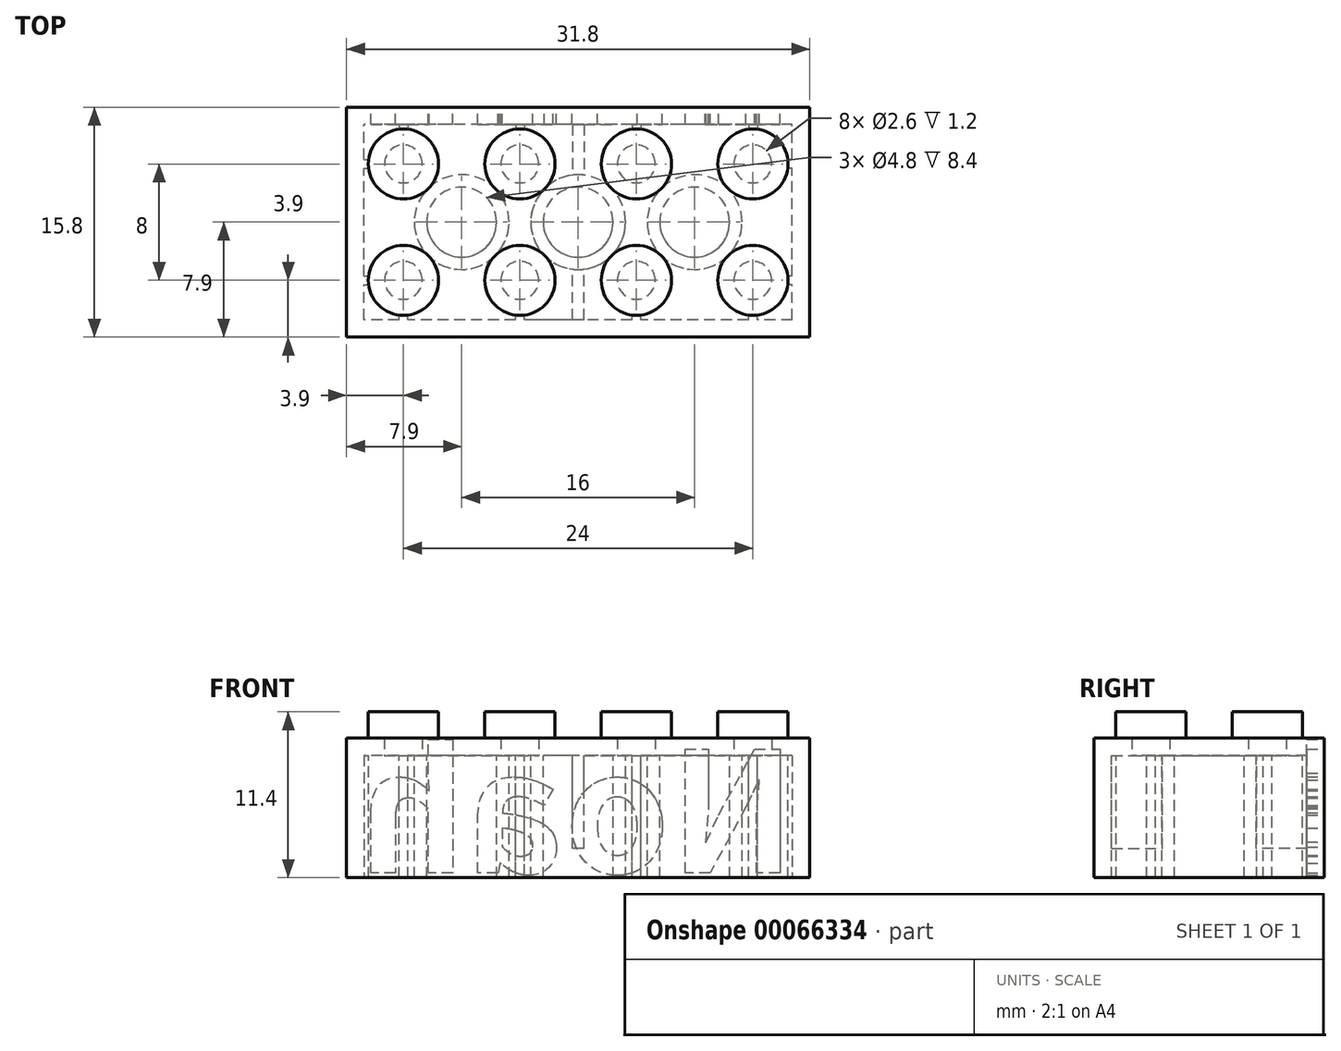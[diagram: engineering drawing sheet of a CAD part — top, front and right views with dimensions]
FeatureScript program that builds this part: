
annotation { "Feature Type Name" : "Feature", "Feature Type Description" : "" }
export const myFeature = defineFeature(function(context is Context, id is Id, definition is map)
    precondition{}
    {
        {
            var Q0;
            Q0=qCreatedBy(makeId("Top.planeOp"),FACE);
            var sketch = newSketch(context, id + "F0", { "sketchPlane" : qUnion([Q0])});
            skLineSegment(sketch, "E0.bottom", {"start": v(-15.9, -7.9) * mm, "end": v(15.9, -7.9) * mm});
            skLineSegment(sketch, "E0.top", {"start": v(-15.9, 7.9) * mm, "end": v(15.9, 7.9) * mm});
            skLineSegment(sketch, "E0.left", {"start": v(-15.9, -7.9) * mm, "end": v(-15.9, 7.9) * mm});
            skLineSegment(sketch, "E0.right", {"start": v(15.9, -7.9) * mm, "end": v(15.9, 7.9) * mm});
            skSolve(sketch);
        }
        {
            var Q0;
            Q0 = qSketchRegion(id + "F0", true);
            extrude(context, id + "F1", {"entities" : qUnion([Q0]), "endBound" : BoundingType.SYMMETRIC, "oppositeDirection" : true, "depth" : 9.6 * mm, "offsetDistance" : 25 * mm});
        }
        {
            var Q0;
            Q0=makeQuery(id+"F1.opExtrude","CAP_FACE",FACE,{"disambiguationData":[OSD([sQuery(id+"F0.wireOp",EDGE,"E0.bottom"),sQuery(id+"F0.wireOp",EDGE,"E0.top"),sQuery(id+"F0.wireOp",EDGE,"E0.left"),sQuery(id+"F0.wireOp",EDGE,"E0.right")])],"isStart":false});
            var sketch = newSketch(context, id + "F2", { "sketchPlane" : qUnion([Q0])});
            skLineSegment(sketch, "E1.bottom", {"start": v(14.7, 6.7) * mm, "end": v(-14.7, 6.7) * mm});
            skLineSegment(sketch, "E1.top", {"start": v(14.7, -6.7) * mm, "end": v(-14.7, -6.7) * mm});
            skLineSegment(sketch, "E1.left", {"start": v(14.7, 6.7) * mm, "end": v(14.7, -6.7) * mm});
            skLineSegment(sketch, "E1.right", {"start": v(-14.7, 6.7) * mm, "end": v(-14.7, -6.7) * mm});
            skPoint(sketch, "E1.middle", {"position": v(0, 0) * mm});
            skSolve(sketch);
        }
        {
            var Q0;
            Q0 = qSketchRegion(id + "F2", true);
            extrude(context, id + "F3", {"entities" : qUnion([Q0]), "operationType" : NewBodyOperationType.REMOVE, "oppositeDirection" : true, "depth" : 8.4 * mm, "offsetDistance" : 25 * mm});
        }
        {
            var Q0;
            Q0=makeQuery(id+"F1.opExtrude","CAP_FACE",FACE,{"disambiguationData":[OSD([sQuery(id+"F0.wireOp",EDGE,"E0.bottom"),sQuery(id+"F0.wireOp",EDGE,"E0.top"),sQuery(id+"F0.wireOp",EDGE,"E0.left"),sQuery(id+"F0.wireOp",EDGE,"E0.right")])],"isStart":true});
            var sketch = newSketch(context, id + "F4", { "sketchPlane" : qUnion([Q0])});
            skCircle(sketch, "E2", {"center": v(-12, 4) * mm, "radius": 2.4 * mm});
            skCircle(sketch, "E3", {"center": v(-4, 4) * mm, "radius": 2.4 * mm});
            skCircle(sketch, "E4.MirrorC", {"center": v(-12, -4) * mm, "radius": 2.4 * mm});
            skCircle(sketch, "E5.MirrorC", {"center": v(-4, -4) * mm, "radius": 2.4 * mm});
            skCircle(sketch, "E6.MirrorC", {"center": v(4, -4) * mm, "radius": 2.4 * mm});
            skCircle(sketch, "E7.MirrorC", {"center": v(12, -4) * mm, "radius": 2.4 * mm});
            skCircle(sketch, "E8.MirrorC", {"center": v(4, 4) * mm, "radius": 2.4 * mm});
            skCircle(sketch, "E9.MirrorC", {"center": v(12, 4) * mm, "radius": 2.4 * mm});
            skSolve(sketch);
        }
        {
            var Q0;
            Q0 = qSketchRegion(id + "F4", true);
            extrude(context, id + "F5", {"entities" : qUnion([Q0]), "operationType" : NewBodyOperationType.ADD, "depth" : 1.8 * mm, "offsetDistance" : 25 * mm});
        }
        {
            var Q0;
            Q0=makeQuery(id+"F3.boolean.opBoolean","COPY",FACE,{"derivedFrom":makeQuery(id+"F3.opExtrude","CAP_FACE",FACE,{"disambiguationData":[OSD([sQuery(id+"F2.wireOp",EDGE,"E1.bottom"),sQuery(id+"F2.wireOp",EDGE,"E1.top"),sQuery(id+"F2.wireOp",EDGE,"E1.left"),sQuery(id+"F2.wireOp",EDGE,"E1.right")])],"isStart":false})});
            var sketch = newSketch(context, id + "F6", { "sketchPlane" : qUnion([Q0])});
            skCircle(sketch, "E10", {"center": v(-12, 4) * mm, "radius": 1.3 * mm});
            skCircle(sketch, "E11", {"center": v(-4, 4) * mm, "radius": 1.3 * mm});
            skCircle(sketch, "E12.MirrorC", {"center": v(-12, -4) * mm, "radius": 1.3 * mm});
            skCircle(sketch, "E13.MirrorC", {"center": v(-4, -4) * mm, "radius": 1.3 * mm});
            skCircle(sketch, "E14.MirrorC", {"center": v(4, -4) * mm, "radius": 1.3 * mm});
            skCircle(sketch, "E15.MirrorC", {"center": v(12, -4) * mm, "radius": 1.3 * mm});
            skCircle(sketch, "E16.MirrorC", {"center": v(4, 4) * mm, "radius": 1.3 * mm});
            skCircle(sketch, "E17.MirrorC", {"center": v(12, 4) * mm, "radius": 1.3 * mm});
            skSolve(sketch);
        }
        {
            var Q0;
            Q0 = qSketchRegion(id + "F6", true);
            extrude(context, id + "F7", {"entities" : qUnion([Q0]), "operationType" : NewBodyOperationType.REMOVE, "oppositeDirection" : true, "depth" : 1.2 * mm, "offsetDistance" : 25 * mm});
        }
        {
            var Q0;
            Q0=makeQuery(id+"F3.boolean.opBoolean","COPY",FACE,{"derivedFrom":makeQuery(id+"F3.opExtrude","CAP_FACE",FACE,{"disambiguationData":[OSD([sQuery(id+"F2.wireOp",EDGE,"E1.bottom"),sQuery(id+"F2.wireOp",EDGE,"E1.top"),sQuery(id+"F2.wireOp",EDGE,"E1.left"),sQuery(id+"F2.wireOp",EDGE,"E1.right")])],"isStart":false})});
            var sketch = newSketch(context, id + "F8", { "sketchPlane" : qUnion([Q0])});
            skPoint(sketch, "E18", {"position": v(-12, 4) * mm});
            skPoint(sketch, "E19", {"position": v(-12, -4) * mm});
            skPoint(sketch, "E20", {"position": v(-4, 4) * mm});
            skPoint(sketch, "E21", {"position": v(-4, -4) * mm});
            skPoint(sketch, "E22", {"position": v(4, 4) * mm});
            skPoint(sketch, "E23", {"position": v(4, -4) * mm});
            skPoint(sketch, "E24", {"position": v(12, 4) * mm});
            skPoint(sketch, "E25", {"position": v(12, -4) * mm});
            skLineSegment(sketch, "E26", {"start": v(-12, 4) * mm, "end": v(-4, -4) * mm, "construction": true});
            skLineSegment(sketch, "E27", {"start": v(-12, -4) * mm, "end": v(-4, 4) * mm, "construction": true});
            skLineSegment(sketch, "E28", {"start": v(-4, 4) * mm, "end": v(4, -4) * mm, "construction": true});
            skLineSegment(sketch, "E29", {"start": v(-4, -4) * mm, "end": v(4, 4) * mm, "construction": true});
            skLineSegment(sketch, "E30", {"start": v(4, 4) * mm, "end": v(12, -4) * mm, "construction": true});
            skLineSegment(sketch, "E31", {"start": v(4, -4) * mm, "end": v(12, 4) * mm, "construction": true});
            skCircle(sketch, "E32", {"center": v(-8, 0) * mm, "radius": 3.25 * mm});
            skCircle(sketch, "E33", {"center": v(0, 0) * mm, "radius": 3.25 * mm});
            skCircle(sketch, "E34", {"center": v(8, 0) * mm, "radius": 3.25 * mm});
            skCircle(sketch, "E35", {"center": v(-8, 0) * mm, "radius": 2.4 * mm});
            skCircle(sketch, "E36", {"center": v(0, 0) * mm, "radius": 2.4 * mm});
            skCircle(sketch, "E37", {"center": v(8, 0) * mm, "radius": 2.4 * mm});
            skSolve(sketch);
        }
        {
            var Q0;
            Q0 = qSketchRegion(id + "F8", true);
            var Q1;
            Q1=makeQuery(id+"F1.opExtrude","CAP_FACE",FACE,{"disambiguationData":[OSD([sQuery(id+"F0.wireOp",EDGE,"E0.bottom"),sQuery(id+"F0.wireOp",EDGE,"E0.top"),sQuery(id+"F0.wireOp",EDGE,"E0.left"),sQuery(id+"F0.wireOp",EDGE,"E0.right")])],"isStart":false});
            extrude(context, id + "F9", {"entities" : qUnion([Q0]), "operationType" : NewBodyOperationType.ADD, "endBound" : BoundingType.UP_TO_SURFACE, "depth" : 25 * mm, "endBoundEntityFace" : qUnion([Q1]), "offsetDistance" : 25 * mm});
        }
        {
            var Q0;
            {var subQ0=sQuery(id+"F2.wireOp",EDGE,"E1.left");var subQ1=sQuery(id+"F2.wireOp",EDGE,"E1.bottom");var subQ2=sQuery(id+"F2.wireOp",EDGE,"E1.top");var subQ3=sQuery(id+"F2.wireOp",EDGE,"E1.right");Q0=makeQuery(id+"F9.boolean.opBoolean","SPLIT",FACE,{"disambiguationData":[TD([makeQuery(id+"F3.boolean.opBoolean","COPY",FACE,{"derivedFrom":makeQuery(id+"F3.opExtrude","SWEPT_FACE",FACE,{"disambiguationData":[OSD([subQ1])]})})])],"derivedFrom":makeQuery(id+"F3.boolean.opBoolean","COPY",FACE,{"derivedFrom":makeQuery(id+"F3.opExtrude","CAP_FACE",FACE,{"disambiguationData":[OSD([subQ1,subQ2,subQ0,subQ3])],"isStart":false})})});}
            var sketch = newSketch(context, id + "F10", { "sketchPlane" : qUnion([Q0])});
            skPoint(sketch, "E38", {"position": v(-12, 4) * mm});
            skLineSegment(sketch, "E39", {"start": v(-12, 4) * mm, "end": v(-24.8, 4) * mm, "construction": true});
            skLineSegment(sketch, "E40.bottom", {"start": v(-14.7, 3.7) * mm, "end": v(-14.4, 3.7) * mm});
            skLineSegment(sketch, "E40.top", {"start": v(-14.7, 4.3) * mm, "end": v(-14.4, 4.3) * mm});
            skLineSegment(sketch, "E40.left", {"start": v(-14.7, 3.7) * mm, "end": v(-14.7, 4.3) * mm});
            skLineSegment(sketch, "E40.right", {"start": v(-14.4, 3.7) * mm, "end": v(-14.4, 4.3) * mm});
            skLineSegment(sketch, "E41.MirrorCS", {"start": v(-14.7, -4.3) * mm, "end": v(-14.4, -4.3) * mm});
            skLineSegment(sketch, "E42.MirrorCS", {"start": v(-14.7, -3.7) * mm, "end": v(-14.7, -4.3) * mm});
            skLineSegment(sketch, "E43.MirrorCS", {"start": v(-14.4, -3.7) * mm, "end": v(-14.4, -4.3) * mm});
            skLineSegment(sketch, "E44.MirrorCS", {"start": v(-14.7, -3.7) * mm, "end": v(-14.4, -3.7) * mm});
            skLineSegment(sketch, "E45.MirrorCS", {"start": v(14.7, 3.7) * mm, "end": v(14.7, 4.3) * mm});
            skLineSegment(sketch, "E46.MirrorCS", {"start": v(14.7, 4.3) * mm, "end": v(14.4, 4.3) * mm});
            skLineSegment(sketch, "E47.MirrorCS", {"start": v(14.4, 3.7) * mm, "end": v(14.4, 4.3) * mm});
            skLineSegment(sketch, "E48.MirrorCS", {"start": v(14.7, 3.7) * mm, "end": v(14.4, 3.7) * mm});
            skLineSegment(sketch, "E49.MirrorCS", {"start": v(14.7, -3.7) * mm, "end": v(14.7, -4.3) * mm});
            skLineSegment(sketch, "E50.MirrorCS", {"start": v(14.7, -3.7) * mm, "end": v(14.4, -3.7) * mm});
            skLineSegment(sketch, "E51.MirrorCS", {"start": v(14.4, -3.7) * mm, "end": v(14.4, -4.3) * mm});
            skLineSegment(sketch, "E52.MirrorCS", {"start": v(14.7, -4.3) * mm, "end": v(14.4, -4.3) * mm});
            skSolve(sketch);
        }
        {
            var Q0;
            Q0 = qSketchRegion(id + "F10", true);
            var Q1;
            Q1=makeQuery(id+"F1.opExtrude","CAP_FACE",FACE,{"disambiguationData":[OSD([sQuery(id+"F0.wireOp",EDGE,"E0.bottom"),sQuery(id+"F0.wireOp",EDGE,"E0.top"),sQuery(id+"F0.wireOp",EDGE,"E0.left"),sQuery(id+"F0.wireOp",EDGE,"E0.right")])],"isStart":false});
            extrude(context, id + "F11", {"entities" : qUnion([Q0]), "operationType" : NewBodyOperationType.ADD, "endBound" : BoundingType.UP_TO_SURFACE, "depth" : 25 * mm, "endBoundEntityFace" : qUnion([Q1]), "offsetDistance" : 25 * mm});
        }
        {
            var Q0;
            {var subQ0=sQuery(id+"F2.wireOp",EDGE,"E1.left");var subQ1=sQuery(id+"F2.wireOp",EDGE,"E1.bottom");var subQ2=sQuery(id+"F2.wireOp",EDGE,"E1.top");var subQ3=sQuery(id+"F2.wireOp",EDGE,"E1.right");Q0=makeQuery(id+"F9.boolean.opBoolean","SPLIT",FACE,{"disambiguationData":[TD([makeQuery(id+"F3.boolean.opBoolean","COPY",FACE,{"derivedFrom":makeQuery(id+"F3.opExtrude","SWEPT_FACE",FACE,{"disambiguationData":[OSD([subQ1])]})})])],"derivedFrom":makeQuery(id+"F3.boolean.opBoolean","COPY",FACE,{"derivedFrom":makeQuery(id+"F3.opExtrude","CAP_FACE",FACE,{"disambiguationData":[OSD([subQ1,subQ2,subQ0,subQ3])],"isStart":false})})});}
            var sketch = newSketch(context, id + "F12", { "sketchPlane" : qUnion([Q0])});
            skPoint(sketch, "E53", {"position": v(-12, 4) * mm});
            skLineSegment(sketch, "E54", {"start": v(-12, 4) * mm, "end": v(-12, 11.14) * mm, "construction": true});
            skLineSegment(sketch, "E55.bottom", {"start": v(-12.3, 6.7) * mm, "end": v(-11.7, 6.7) * mm});
            skLineSegment(sketch, "E55.top", {"start": v(-12.3, 6.4) * mm, "end": v(-11.7, 6.4) * mm});
            skLineSegment(sketch, "E55.left", {"start": v(-12.3, 6.7) * mm, "end": v(-12.3, 6.4) * mm});
            skLineSegment(sketch, "E55.right", {"start": v(-11.7, 6.7) * mm, "end": v(-11.7, 6.4) * mm});
            skPoint(sketch, "E56", {"position": v(-8, 0) * mm});
            skLineSegment(sketch, "E57", {"start": v(-8, 0) * mm, "end": v(-8, 8.75) * mm, "construction": true});
            skLineSegment(sketch, "E58.MirrorCS", {"start": v(-3.7, 6.4) * mm, "end": v(-4.3, 6.4) * mm});
            skLineSegment(sketch, "E59.MirrorCS", {"start": v(-3.7, 6.7) * mm, "end": v(-3.7, 6.4) * mm});
            skLineSegment(sketch, "E60.MirrorCS", {"start": v(-3.7, 6.7) * mm, "end": v(-4.3, 6.7) * mm});
            skLineSegment(sketch, "E61.MirrorCS", {"start": v(-4.3, 6.7) * mm, "end": v(-4.3, 6.4) * mm});
            skLineSegment(sketch, "E62.MirrorCS", {"start": v(12.3, 6.7) * mm, "end": v(12.3, 6.4) * mm});
            skLineSegment(sketch, "E63.MirrorCS", {"start": v(12.3, 6.7) * mm, "end": v(11.7, 6.7) * mm});
            skLineSegment(sketch, "E64.MirrorCS", {"start": v(11.7, 6.7) * mm, "end": v(11.7, 6.4) * mm});
            skLineSegment(sketch, "E65.MirrorCS", {"start": v(12.3, 6.4) * mm, "end": v(11.7, 6.4) * mm});
            skLineSegment(sketch, "E66.MirrorCS", {"start": v(3.7, 6.7) * mm, "end": v(4.3, 6.7) * mm});
            skLineSegment(sketch, "E67.MirrorCS", {"start": v(4.3, 6.7) * mm, "end": v(4.3, 6.4) * mm});
            skLineSegment(sketch, "E68.MirrorCS", {"start": v(3.7, 6.7) * mm, "end": v(3.7, 6.4) * mm});
            skLineSegment(sketch, "E69.MirrorCS", {"start": v(3.7, 6.4) * mm, "end": v(4.3, 6.4) * mm});
            skLineSegment(sketch, "E70.MirrorCS", {"start": v(-12.3, -6.7) * mm, "end": v(-12.3, -6.4) * mm});
            skLineSegment(sketch, "E71.MirrorCS", {"start": v(-12.3, -6.7) * mm, "end": v(-11.7, -6.7) * mm});
            skLineSegment(sketch, "E72.MirrorCS", {"start": v(-12.3, -6.4) * mm, "end": v(-11.7, -6.4) * mm});
            skLineSegment(sketch, "E73.MirrorCS", {"start": v(-11.7, -6.7) * mm, "end": v(-11.7, -6.4) * mm});
            skLineSegment(sketch, "E74.MirrorCS", {"start": v(-4.3, -6.7) * mm, "end": v(-4.3, -6.4) * mm});
            skLineSegment(sketch, "E75.MirrorCS", {"start": v(-3.7, -6.7) * mm, "end": v(-4.3, -6.7) * mm});
            skLineSegment(sketch, "E76.MirrorCS", {"start": v(-3.7, -6.7) * mm, "end": v(-3.7, -6.4) * mm});
            skLineSegment(sketch, "E77.MirrorCS", {"start": v(-3.7, -6.4) * mm, "end": v(-4.3, -6.4) * mm});
            skLineSegment(sketch, "E78.MirrorCS", {"start": v(3.7, -6.7) * mm, "end": v(3.7, -6.4) * mm});
            skLineSegment(sketch, "E79.MirrorCS", {"start": v(3.7, -6.7) * mm, "end": v(4.3, -6.7) * mm});
            skLineSegment(sketch, "E80.MirrorCS", {"start": v(4.3, -6.7) * mm, "end": v(4.3, -6.4) * mm});
            skLineSegment(sketch, "E81.MirrorCS", {"start": v(3.7, -6.4) * mm, "end": v(4.3, -6.4) * mm});
            skLineSegment(sketch, "E82.MirrorCS", {"start": v(11.7, -6.7) * mm, "end": v(11.7, -6.4) * mm});
            skLineSegment(sketch, "E83.MirrorCS", {"start": v(12.3, -6.7) * mm, "end": v(11.7, -6.7) * mm});
            skLineSegment(sketch, "E84.MirrorCS", {"start": v(12.3, -6.7) * mm, "end": v(12.3, -6.4) * mm});
            skLineSegment(sketch, "E85.MirrorCS", {"start": v(12.3, -6.4) * mm, "end": v(11.7, -6.4) * mm});
            skSolve(sketch);
        }
        {
            var Q0;
            Q0 = qSketchRegion(id + "F12", true);
            var Q1;
            {var subQ0=sQuery(id+"F0.wireOp",EDGE,"E0.right");var subQ1=sQuery(id+"F0.wireOp",EDGE,"E0.left");var subQ2=sQuery(id+"F0.wireOp",EDGE,"E0.top");var subQ3=sQuery(id+"F0.wireOp",EDGE,"E0.bottom");Q1=makeQuery(id+"F11.boolean.opBoolean","MERGE",FACE,{"derivedFrom":[makeQuery(id+"F1.opExtrude","CAP_FACE",FACE,{"disambiguationData":[OSD([subQ3,subQ2,subQ1,subQ0])],"isStart":false}),makeQuery(id+"F11.opExtrude","CAP_FACE",FACE,{"disambiguationData":[OSD([subQ3,subQ2,subQ1,subQ0]),OD(0.0)],"isStart":false}),makeQuery(id+"F11.opExtrude","CAP_FACE",FACE,{"disambiguationData":[OSD([subQ3,subQ2,subQ1,subQ0]),OD(1.0)],"isStart":false}),makeQuery(id+"F11.opExtrude","CAP_FACE",FACE,{"disambiguationData":[OSD([subQ3,subQ2,subQ1,subQ0]),OD(2.0)],"isStart":false}),makeQuery(id+"F11.opExtrude","CAP_FACE",FACE,{"disambiguationData":[OSD([subQ3,subQ2,subQ1,subQ0]),OD(3.0)],"isStart":false})]});}
            extrude(context, id + "F13", {"entities" : qUnion([Q0]), "operationType" : NewBodyOperationType.ADD, "endBound" : BoundingType.UP_TO_SURFACE, "depth" : 25 * mm, "endBoundEntityFace" : qUnion([Q1]), "offsetDistance" : 25 * mm});
        }
        {
            var Q0;
            {var subQ0=sQuery(id+"F2.wireOp",EDGE,"E1.left");var subQ1=sQuery(id+"F2.wireOp",EDGE,"E1.bottom");var subQ2=sQuery(id+"F2.wireOp",EDGE,"E1.top");var subQ3=sQuery(id+"F2.wireOp",EDGE,"E1.right");Q0=makeQuery(id+"F9.boolean.opBoolean","SPLIT",FACE,{"disambiguationData":[TD([makeQuery(id+"F3.boolean.opBoolean","COPY",FACE,{"derivedFrom":makeQuery(id+"F3.opExtrude","SWEPT_FACE",FACE,{"disambiguationData":[OSD([subQ1])]})})])],"derivedFrom":makeQuery(id+"F3.boolean.opBoolean","COPY",FACE,{"derivedFrom":makeQuery(id+"F3.opExtrude","CAP_FACE",FACE,{"disambiguationData":[OSD([subQ1,subQ2,subQ0,subQ3])],"isStart":false})})});}
            var sketch = newSketch(context, id + "F14", { "sketchPlane" : qUnion([Q0])});
            skLineSegment(sketch, "E86.bottom", {"start": v(-0.4, 6.7) * mm, "end": v(0.4, 6.7) * mm});
            skLineSegment(sketch, "E86.top", {"start": v(-0.4, 3.23) * mm, "end": v(0.4, 3.23) * mm});
            skLineSegment(sketch, "E86.left", {"start": v(-0.4, 6.7) * mm, "end": v(-0.4, 3.23) * mm});
            skLineSegment(sketch, "E86.right", {"start": v(0.4, 6.7) * mm, "end": v(0.4, 3.23) * mm});
            skLineSegment(sketch, "E87.MirrorCS", {"start": v(-0.4, -6.7) * mm, "end": v(-0.4, -3.23) * mm});
            skLineSegment(sketch, "E88.MirrorCS", {"start": v(-0.4, -6.7) * mm, "end": v(0.4, -6.7) * mm});
            skLineSegment(sketch, "E89.MirrorCS", {"start": v(0.4, -6.7) * mm, "end": v(0.4, -3.23) * mm});
            skLineSegment(sketch, "E90.MirrorCS", {"start": v(-0.4, -3.23) * mm, "end": v(0.4, -3.23) * mm});
            skSolve(sketch);
        }
        {
            var Q0;
            Q0 = qSketchRegion(id + "F14", true);
            extrude(context, id + "F15", {"entities" : qUnion([Q0]), "operationType" : NewBodyOperationType.ADD, "depth" : 6.4 * mm, "offsetDistance" : 25 * mm});
        }
        {
            var Q0;
            Q0=makeQuery(id+"F1.opExtrude","SWEPT_FACE",FACE,{"disambiguationData":[OSD([sQuery(id+"F0.wireOp",EDGE,"E0.top")])]});
            var sketch = newSketch(context, id + "F16", { "sketchPlane" : qUnion([Q0])});
            skText(sketch, "E91", { "text": "Noah", "fontName": "NotoSansCJKtc-Bold.otf"});
            const initialGuessF16  = {"E91": [-0.0149, -0.00448, 1, 0, 0.00828]};
            skSetInitialGuess(sketch, initialGuessF16);
            skSolve(sketch);
        }
        {
            var Q0;
            Q0 = qSketchRegion(id + "F16", true);
            extrude(context, id + "F17", {"entities" : qUnion([Q0]), "operationType" : NewBodyOperationType.REMOVE, "oppositeDirection" : true, "depth" : 1.2 * mm, "offsetDistance" : 25 * mm});
        }
    });
